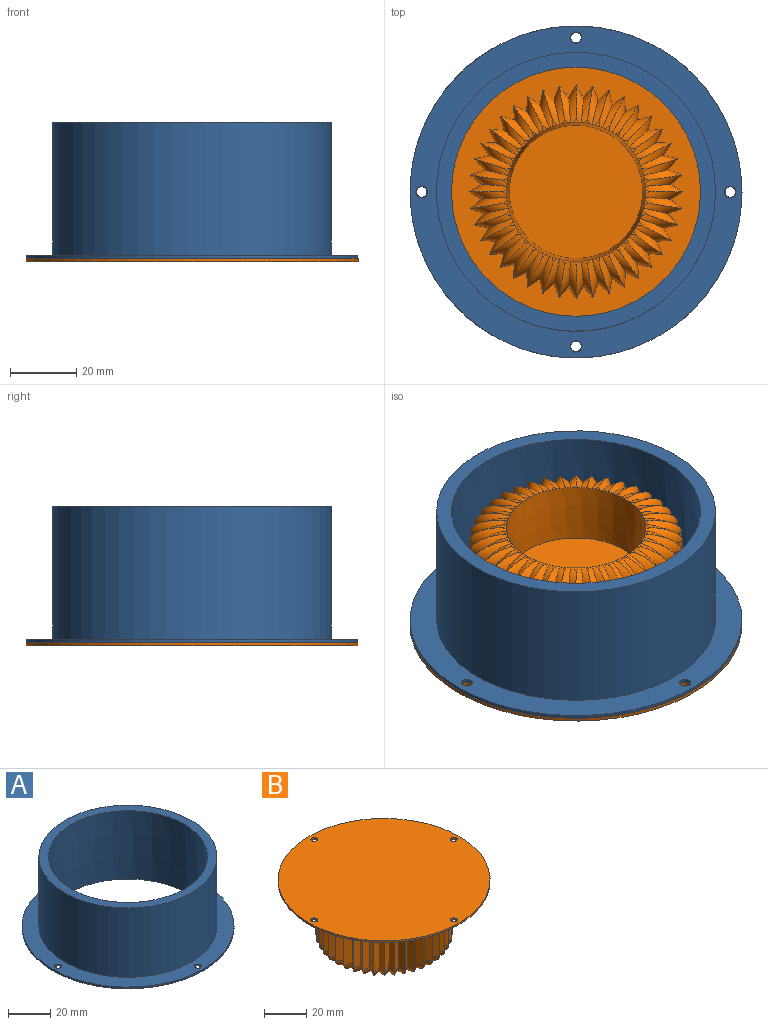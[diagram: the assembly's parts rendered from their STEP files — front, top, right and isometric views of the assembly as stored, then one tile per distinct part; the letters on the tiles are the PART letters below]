
ASSEMBLY  parts=2 mates=1
PART A: 10 faces, bbox 100x100x41 mm
  f0: cylinder r=42mm len=84mm, axis (0,0,-1), area 10555.8mm2, adj f1,f4
  f1: plane 84x84mm, normal (0,0,1), area 1123.9mm2, adj f0,f5
  f2: cylinder r=50mm len=100mm, axis (0,0,1), area 314.2mm2, adj f3,f4
  f3: plane 100x100mm, normal (0,0,-1), area 2879mm2, adj f2,f5,f6,f7,f8,f9
  f4: plane 100x100mm, normal (0,0,1), area 2275.9mm2, adj f0,f2,f6,f7,f8,f9
  f5: cone r=37.5mm half-angle=3deg, axis (0,0,-1), area 9950.8mm2, adj f1,f3
  f6: cylinder r=1.7mm len=3.4mm, axis (0,0,1), area 10.7mm2, adj f3,f4
  f7: cylinder r=1.7mm len=3.4mm, axis (0,0,1), area 10.7mm2, adj f3,f4
  f8: cylinder r=1.7mm len=3.4mm, axis (0,0,1), area 10.7mm2, adj f3,f4
  f9: cylinder r=1.7mm len=3.4mm, axis (0,0,1), area 10.7mm2, adj f3,f4
PART B: 289 faces, bbox 100x100x36 mm
  f0: cylinder r=1.6mm len=3.2mm, axis (0,0,1), area 10.1mm2, adj f285,f287
  f1: cylinder r=1.6mm len=3.2mm, axis (0,0,1), area 10.1mm2, adj f285,f287
  f2: cylinder r=1.6mm len=3.2mm, axis (0,0,1), area 10.1mm2, adj f285,f287
  f3: plane 1.37x1.29mm, normal (0,0,-1), area 0.8mm2, adj f199,f201,f283
  f4: plane 1.35x1.32mm, normal (0,0,-1), area 0.8mm2, adj f195,f197,f283
  f5: plane 1.38x1.23mm, normal (0,0,-1), area 0.8mm2, adj f191,f193,f283
  f6: plane 1.38x1.26mm, normal (0,0,-1), area 0.8mm2, adj f187,f189,f283
  f7: plane 1.34x1.34mm, normal (0,0,-1), area 0.8mm2, adj f183,f185,f283
  f8: plane 1.38x1.26mm, normal (0,0,-1), area 0.8mm2, adj f179,f181,f283
  f9: plane 1.38x1.23mm, normal (0,0,-1), area 0.8mm2, adj f175,f177,f283
  f10: plane 1.35x1.32mm, normal (0,0,-1), area 0.8mm2, adj f171,f173,f283
  f11: plane 1.37x1.29mm, normal (0,0,-1), area 0.8mm2, adj f167,f169,f283
  f12: plane 1.38x1.2mm, normal (0,0,-1), area 0.8mm2, adj f163,f165,f283
  f13: plane 1.37x1.29mm, normal (0,0,-1), area 0.8mm2, adj f159,f161,f283
  f14: plane 1.35x1.32mm, normal (0,0,-1), area 0.8mm2, adj f155,f157,f283
  f15: plane 1.38x1.23mm, normal (0,0,-1), area 0.8mm2, adj f151,f153,f283
  f16: plane 1.38x1.26mm, normal (0,0,-1), area 0.8mm2, adj f147,f149,f283
  f17: plane 1.34x1.34mm, normal (0,0,-1), area 0.8mm2, adj f143,f145,f283
  f18: plane 1.38x1.26mm, normal (0,0,-1), area 0.8mm2, adj f139,f141,f283
  f19: plane 1.38x1.23mm, normal (0,0,-1), area 0.8mm2, adj f135,f137,f283
  f20: plane 1.35x1.32mm, normal (0,0,-1), area 0.8mm2, adj f131,f133,f283
  f21: plane 1.37x1.29mm, normal (0,0,-1), area 0.8mm2, adj f127,f129,f283
  f22: plane 1.38x1.2mm, normal (0,0,-1), area 0.8mm2, adj f123,f125,f283
  f23: plane 1.37x1.29mm, normal (0,0,-1), area 0.8mm2, adj f124,f126,f283
  f24: plane 1.35x1.32mm, normal (0,0,-1), area 0.8mm2, adj f128,f130,f283
  f25: plane 1.38x1.23mm, normal (0,0,-1), area 0.8mm2, adj f132,f134,f283
  f26: plane 1.38x1.26mm, normal (0,0,-1), area 0.8mm2, adj f136,f138,f283
  f27: plane 1.34x1.34mm, normal (0,0,-1), area 0.8mm2, adj f140,f142,f283
  f28: plane 1.38x1.26mm, normal (0,0,-1), area 0.8mm2, adj f144,f146,f283
  f29: plane 1.38x1.23mm, normal (0,0,-1), area 0.8mm2, adj f148,f150,f283
  f30: plane 1.35x1.32mm, normal (0,0,-1), area 0.8mm2, adj f152,f154,f283
  f31: plane 1.37x1.29mm, normal (0,0,-1), area 0.8mm2, adj f156,f158,f283
  f32: plane 1.38x1.2mm, normal (0,0,-1), area 0.8mm2, adj f160,f162,f283
  f33: plane 1.37x1.29mm, normal (0,0,-1), area 0.8mm2, adj f164,f166,f283
  f34: plane 1.35x1.32mm, normal (0,0,-1), area 0.8mm2, adj f168,f170,f283
  f35: plane 1.38x1.23mm, normal (0,0,-1), area 0.8mm2, adj f172,f174,f283
  f36: plane 1.38x1.26mm, normal (0,0,-1), area 0.8mm2, adj f176,f178,f283
  f37: plane 1.34x1.34mm, normal (0,0,-1), area 0.8mm2, adj f180,f182,f283
  f38: plane 1.38x1.26mm, normal (0,0,-1), area 0.8mm2, adj f184,f186,f283
  f39: plane 1.38x1.23mm, normal (0,0,-1), area 0.8mm2, adj f188,f190,f283
  f40: plane 1.35x1.32mm, normal (0,0,-1), area 0.8mm2, adj f192,f194,f283
  f41: plane 1.37x1.29mm, normal (0,0,-1), area 0.8mm2, adj f196,f198,f283
  f42: plane 1.38x1.2mm, normal (0,0,-1), area 0.8mm2, adj f200,f202,f283
  f43: plane 25x3.86mm, normal (-0.5,-0.87,0), area 111.5mm2, adj f44,f122,f200,f280
  f44: plane 25x3.47mm, normal (-0.63,0.78,0), area 111.5mm2, adj f43,f45,f198,f278
  f45: plane 25x4.16mm, normal (-0.36,-0.93,0), area 111.5mm2, adj f44,f46,f196,f276
  f46: plane 25x3.31mm, normal (-0.74,0.67,0), area 111.5mm2, adj f45,f47,f194,f274
  f47: plane 25x4.36mm, normal (-0.21,-0.98,0), area 111.5mm2, adj f46,f48,f192,f272
  f48: plane 25x3.74mm, normal (-0.84,0.54,0), area 111.5mm2, adj f47,f49,f190,f270
  f49: plane 25x4.45mm, normal (-0.05,-1,0), area 111.5mm2, adj f48,f50,f188,f268
  f50: plane 25x4.07mm, normal (-0.91,0.41,0), area 111.5mm2, adj f49,f51,f186,f266
  f51: plane 25x4.43mm, normal (0.1,-0.99,0), area 111.5mm2, adj f50,f52,f184,f264
  f52: plane 25x4.31mm, normal (-0.97,0.26,0), area 111.5mm2, adj f51,f53,f182,f262
  f53: plane 25x4.31mm, normal (0.26,-0.97,0), area 111.5mm2, adj f52,f54,f180,f260
  f54: plane 25x4.43mm, normal (-0.99,0.1,0), area 111.5mm2, adj f53,f55,f178,f258
  f55: plane 25x4.07mm, normal (0.41,-0.91,0), area 111.5mm2, adj f54,f56,f176,f256
  f56: plane 25x4.45mm, normal (-1,-0.05,0), area 111.5mm2, adj f55,f57,f174,f254
  f57: plane 25x3.74mm, normal (0.54,-0.84,0), area 111.5mm2, adj f56,f58,f172,f252
  f58: plane 25x4.36mm, normal (-0.98,-0.21,0), area 111.5mm2, adj f57,f59,f170,f250
  f59: plane 25x3.31mm, normal (0.67,-0.74,0), area 111.5mm2, adj f58,f60,f168,f248
  f60: plane 25x4.16mm, normal (-0.93,-0.36,0), area 111.5mm2, adj f59,f61,f166,f246
  f61: plane 25x3.47mm, normal (0.78,-0.63,0), area 111.5mm2, adj f60,f62,f164,f244
  f62: plane 25x3.86mm, normal (-0.87,-0.5,0), area 111.5mm2, adj f61,f63,f162,f242
  f63: plane 25x3.86mm, normal (0.87,-0.5,0), area 111.5mm2, adj f62,f64,f160,f240
  f64: plane 25x3.47mm, normal (-0.78,-0.63,0), area 111.5mm2, adj f63,f65,f158,f238
  f65: plane 25x4.16mm, normal (0.93,-0.36,0), area 111.5mm2, adj f64,f66,f156,f236
  f66: plane 25x3.31mm, normal (-0.67,-0.74,0), area 111.5mm2, adj f65,f67,f154,f234
  f67: plane 25x4.36mm, normal (0.98,-0.21,0), area 111.5mm2, adj f66,f68,f152,f232
  f68: plane 25x3.74mm, normal (-0.54,-0.84,0), area 111.5mm2, adj f67,f69,f150,f230
  f69: plane 25x4.45mm, normal (1,-0.05,0), area 111.5mm2, adj f68,f70,f148,f228
  f70: plane 25x4.07mm, normal (-0.41,-0.91,0), area 111.5mm2, adj f69,f71,f146,f226
  f71: plane 25x4.43mm, normal (0.99,0.1,0), area 111.5mm2, adj f70,f72,f144,f224
  f72: plane 25x4.31mm, normal (-0.26,-0.97,0), area 111.5mm2, adj f71,f73,f142,f222
  f73: plane 25x4.31mm, normal (0.97,0.26,0), area 111.5mm2, adj f72,f74,f140,f220
  f74: plane 25x4.43mm, normal (-0.1,-0.99,0), area 111.5mm2, adj f73,f75,f138,f218
  f75: plane 25x4.07mm, normal (0.91,0.41,0), area 111.5mm2, adj f74,f76,f136,f216
  f76: plane 25x4.45mm, normal (0.05,-1,0), area 111.5mm2, adj f75,f77,f134,f214
  f77: plane 25x3.74mm, normal (0.84,0.54,0), area 111.5mm2, adj f76,f78,f132,f212
  f78: plane 25x4.36mm, normal (0.21,-0.98,0), area 111.5mm2, adj f77,f79,f130,f210
  f79: plane 25x3.31mm, normal (0.74,0.67,0), area 111.5mm2, adj f78,f80,f128,f208
  f80: plane 25x4.16mm, normal (0.36,-0.93,0), area 111.5mm2, adj f79,f81,f126,f206
  f81: plane 25x3.47mm, normal (0.63,0.78,0), area 111.5mm2, adj f80,f82,f124,f204
  f82: plane 25x3.86mm, normal (0.5,-0.87,0), area 111.5mm2, adj f81,f83,f123,f203
  f83: plane 25x3.86mm, normal (0.5,0.87,0), area 111.5mm2, adj f82,f84,f125,f205
  f84: plane 25x3.47mm, normal (0.63,-0.78,0), area 111.5mm2, adj f83,f85,f127,f207
  f85: plane 25x4.16mm, normal (0.36,0.93,0), area 111.5mm2, adj f84,f86,f129,f209
  f86: plane 25x3.31mm, normal (0.74,-0.67,0), area 111.5mm2, adj f85,f87,f131,f211
  f87: plane 25x4.36mm, normal (0.21,0.98,0), area 111.5mm2, adj f86,f88,f133,f213
  f88: plane 25x3.74mm, normal (0.84,-0.54,0), area 111.5mm2, adj f87,f89,f135,f215
  f89: plane 25x4.45mm, normal (0.05,1,0), area 111.5mm2, adj f88,f90,f137,f217
  f90: plane 25x4.07mm, normal (0.91,-0.41,0), area 111.5mm2, adj f89,f91,f139,f219
  f91: plane 25x4.43mm, normal (-0.1,0.99,0), area 111.5mm2, adj f90,f92,f141,f221
  f92: plane 25x4.31mm, normal (0.97,-0.26,0), area 111.5mm2, adj f91,f93,f143,f223
  f93: plane 25x4.31mm, normal (-0.26,0.97,0), area 111.5mm2, adj f92,f94,f145,f225
  f94: plane 25x4.43mm, normal (0.99,-0.1,0), area 111.5mm2, adj f93,f95,f147,f227
  f95: plane 25x4.07mm, normal (-0.41,0.91,0), area 111.5mm2, adj f94,f96,f149,f229
  f96: plane 25x4.45mm, normal (1,0.05,0), area 111.5mm2, adj f95,f97,f151,f231
  f97: plane 25x3.74mm, normal (-0.54,0.84,0), area 111.5mm2, adj f96,f98,f153,f233
  f98: plane 25x4.36mm, normal (0.98,0.21,0), area 111.5mm2, adj f97,f99,f155,f235
  f99: plane 25x3.31mm, normal (-0.67,0.74,0), area 111.5mm2, adj f98,f100,f157,f237
  f100: plane 25x4.16mm, normal (0.93,0.36,0), area 111.5mm2, adj f99,f101,f159,f239
  f101: plane 25x3.47mm, normal (-0.78,0.63,0), area 111.5mm2, adj f100,f102,f161,f241
  f102: plane 25x3.86mm, normal (0.87,0.5,0), area 111.5mm2, adj f101,f103,f163,f243
  f103: plane 25x3.86mm, normal (-0.87,0.5,0), area 111.5mm2, adj f102,f104,f165,f245
  f104: plane 25x3.47mm, normal (0.78,0.63,0), area 111.5mm2, adj f103,f105,f167,f247
  f105: plane 25x4.16mm, normal (-0.93,0.36,0), area 111.5mm2, adj f104,f106,f169,f249
  f106: plane 25x3.31mm, normal (0.67,0.74,0), area 111.5mm2, adj f105,f107,f171,f251
  f107: plane 25x4.36mm, normal (-0.98,0.21,0), area 111.5mm2, adj f106,f108,f173,f253
  f108: plane 25x3.74mm, normal (0.54,0.84,0), area 111.5mm2, adj f107,f109,f175,f255
  f109: plane 25x4.45mm, normal (-1,0.05,0), area 111.5mm2, adj f108,f110,f177,f257
  f110: plane 25x4.07mm, normal (0.41,0.91,0), area 111.5mm2, adj f109,f111,f179,f259
  f111: plane 25x4.43mm, normal (-0.99,-0.1,0), area 111.5mm2, adj f110,f112,f181,f261
  f112: plane 25x4.31mm, normal (0.26,0.97,0), area 111.5mm2, adj f111,f113,f183,f263
  f113: plane 25x4.31mm, normal (-0.97,-0.26,0), area 111.5mm2, adj f112,f114,f185,f265
  f114: plane 25x4.43mm, normal (0.1,0.99,0), area 111.5mm2, adj f113,f115,f187,f267
  f115: plane 25x4.07mm, normal (-0.91,-0.41,0), area 111.5mm2, adj f114,f116,f189,f269
  f116: plane 25x4.45mm, normal (-0.05,1,0), area 111.5mm2, adj f115,f117,f191,f271
  f117: plane 25x3.74mm, normal (-0.84,-0.54,0), area 111.5mm2, adj f116,f118,f193,f273
  f118: plane 25x4.36mm, normal (-0.21,0.98,0), area 111.5mm2, adj f117,f119,f195,f275
  f119: plane 25x3.31mm, normal (-0.74,-0.67,0), area 111.5mm2, adj f118,f120,f197,f277
  f120: plane 25x4.16mm, normal (-0.36,0.93,0), area 111.5mm2, adj f119,f121,f199,f279
  f121: plane 25x3.47mm, normal (-0.63,-0.78,0), area 111.5mm2, adj f120,f122,f201,f281
  f122: plane 25x3.86mm, normal (-0.5,0.87,0), area 111.5mm2, adj f43,f121,f202,f282
  f123: cylinder r=5mm len=11.65mm, axis (0.87,0.5,0), area 30.4mm2, adj f22,f82,f124,f125,f283
  f124: cylinder r=5mm len=11.36mm, axis (-0.78,0.63,0), area 30.4mm2, adj f23,f81,f123,f126,f283
  f125: cylinder r=5mm len=11.65mm, axis (-0.87,0.5,0), area 30.4mm2, adj f22,f83,f123,f127,f283
  f126: cylinder r=5mm len=11.66mm, axis (0.93,0.36,0), area 30.4mm2, adj f23,f80,f124,f128,f283
  f127: cylinder r=5mm len=11.36mm, axis (0.78,0.63,0), area 30.4mm2, adj f21,f84,f125,f129,f283
  f128: cylinder r=5mm len=11.2mm, axis (-0.67,0.74,0), area 30.4mm2, adj f24,f79,f126,f130,f283
  f129: cylinder r=5mm len=11.66mm, axis (-0.93,0.36,0), area 30.4mm2, adj f21,f85,f127,f131,f283
  f130: cylinder r=5mm len=11.38mm, axis (0.98,0.21,0), area 30.4mm2, adj f24,f78,f128,f132,f283
  f131: cylinder r=5mm len=11.2mm, axis (0.67,0.74,0), area 30.4mm2, adj f20,f86,f129,f133,f283
  f132: cylinder r=5mm len=11.59mm, axis (-0.54,0.84,0), area 30.4mm2, adj f25,f77,f130,f134,f283
  f133: cylinder r=5mm len=11.38mm, axis (-0.98,0.21,0), area 30.4mm2, adj f20,f87,f131,f135,f283
  f134: cylinder r=5mm len=10.82mm, axis (1,0.05,0), area 30.4mm2, adj f25,f76,f132,f136,f283
  f135: cylinder r=5mm len=11.59mm, axis (0.54,0.84,0), area 30.4mm2, adj f19,f88,f133,f137,f283
  f136: cylinder r=5mm len=11.69mm, axis (-0.41,0.91,0), area 30.4mm2, adj f26,f75,f134,f138,f283
  f137: cylinder r=5mm len=10.82mm, axis (-1,0.05,0), area 30.4mm2, adj f19,f89,f135,f139,f283
  f138: cylinder r=5mm len=11.04mm, axis (0.99,-0.1,0), area 30.4mm2, adj f26,f74,f136,f140,f283
  f139: cylinder r=5mm len=11.69mm, axis (0.41,0.91,0), area 30.4mm2, adj f18,f90,f137,f141,f283
  f140: cylinder r=5mm len=11.5mm, axis (-0.26,0.97,0), area 30.4mm2, adj f27,f73,f138,f142,f283
  f141: cylinder r=5mm len=11.04mm, axis (-0.99,-0.1,0), area 30.4mm2, adj f18,f91,f139,f143,f283
  f142: cylinder r=5mm len=11.5mm, axis (0.97,-0.26,0), area 30.4mm2, adj f27,f72,f140,f144,f283
  f143: cylinder r=5mm len=11.5mm, axis (0.26,0.97,0), area 30.4mm2, adj f17,f92,f141,f145,f283
  f144: cylinder r=5mm len=11.04mm, axis (-0.1,0.99,0), area 30.4mm2, adj f28,f71,f142,f146,f283
  f145: cylinder r=5mm len=11.5mm, axis (-0.97,-0.26,0), area 30.4mm2, adj f17,f93,f143,f147,f283
  f146: cylinder r=5mm len=11.69mm, axis (0.91,-0.41,0), area 30.4mm2, adj f28,f70,f144,f148,f283
  f147: cylinder r=5mm len=11.04mm, axis (0.1,0.99,0), area 30.4mm2, adj f16,f94,f145,f149,f283
  f148: cylinder r=5mm len=10.82mm, axis (0.05,1,0), area 30.4mm2, adj f29,f69,f146,f150,f283
  f149: cylinder r=5mm len=11.69mm, axis (-0.91,-0.41,0), area 30.4mm2, adj f16,f95,f147,f151,f283
  f150: cylinder r=5mm len=11.59mm, axis (0.84,-0.54,0), area 30.4mm2, adj f29,f68,f148,f152,f283
  f151: cylinder r=5mm len=10.82mm, axis (-0.05,1,0), area 30.4mm2, adj f15,f96,f149,f153,f283
  f152: cylinder r=5mm len=11.38mm, axis (0.21,0.98,0), area 30.4mm2, adj f30,f67,f150,f154,f283
  f153: cylinder r=5mm len=11.59mm, axis (-0.84,-0.54,0), area 30.4mm2, adj f15,f97,f151,f155,f283
  f154: cylinder r=5mm len=11.2mm, axis (0.74,-0.67,0), area 30.4mm2, adj f30,f66,f152,f156,f283
  f155: cylinder r=5mm len=11.38mm, axis (-0.21,0.98,0), area 30.4mm2, adj f14,f98,f153,f157,f283
  f156: cylinder r=5mm len=11.66mm, axis (0.36,0.93,0), area 30.4mm2, adj f31,f65,f154,f158,f283
  f157: cylinder r=5mm len=11.2mm, axis (-0.74,-0.67,0), area 30.4mm2, adj f14,f99,f155,f159,f283
  f158: cylinder r=5mm len=11.36mm, axis (0.63,-0.78,0), area 30.4mm2, adj f31,f64,f156,f160,f283
  f159: cylinder r=5mm len=11.66mm, axis (-0.36,0.93,0), area 30.4mm2, adj f13,f100,f157,f161,f283
  f160: cylinder r=5mm len=11.65mm, axis (0.5,0.87,0), area 30.4mm2, adj f32,f63,f158,f162,f283
  f161: cylinder r=5mm len=11.36mm, axis (-0.63,-0.78,0), area 30.4mm2, adj f13,f101,f159,f163,f283
  f162: cylinder r=5mm len=11.65mm, axis (0.5,-0.87,0), area 30.4mm2, adj f32,f62,f160,f164,f283
  f163: cylinder r=5mm len=11.65mm, axis (-0.5,0.87,0), area 30.4mm2, adj f12,f102,f161,f165,f283
  f164: cylinder r=5mm len=11.36mm, axis (0.63,0.78,0), area 30.4mm2, adj f33,f61,f162,f166,f283
  f165: cylinder r=5mm len=11.65mm, axis (-0.5,-0.87,0), area 30.4mm2, adj f12,f103,f163,f167,f283
  f166: cylinder r=5mm len=11.66mm, axis (0.36,-0.93,0), area 30.4mm2, adj f33,f60,f164,f168,f283
  f167: cylinder r=5mm len=11.36mm, axis (-0.63,0.78,0), area 30.4mm2, adj f11,f104,f165,f169,f283
  f168: cylinder r=5mm len=11.2mm, axis (0.74,0.67,0), area 30.4mm2, adj f34,f59,f166,f170,f283
  f169: cylinder r=5mm len=11.66mm, axis (-0.36,-0.93,0), area 30.4mm2, adj f11,f105,f167,f171,f283
  f170: cylinder r=5mm len=11.38mm, axis (0.21,-0.98,0), area 30.4mm2, adj f34,f58,f168,f172,f283
  f171: cylinder r=5mm len=11.2mm, axis (-0.74,0.67,0), area 30.4mm2, adj f10,f106,f169,f173,f283
  f172: cylinder r=5mm len=11.59mm, axis (0.84,0.54,0), area 30.4mm2, adj f35,f57,f170,f174,f283
  f173: cylinder r=5mm len=11.38mm, axis (-0.21,-0.98,0), area 30.4mm2, adj f10,f107,f171,f175,f283
  f174: cylinder r=5mm len=10.82mm, axis (0.05,-1,0), area 30.4mm2, adj f35,f56,f172,f176,f283
  f175: cylinder r=5mm len=11.59mm, axis (-0.84,0.54,0), area 30.4mm2, adj f9,f108,f173,f177,f283
  f176: cylinder r=5mm len=11.69mm, axis (0.91,0.41,0), area 30.4mm2, adj f36,f55,f174,f178,f283
  f177: cylinder r=5mm len=10.82mm, axis (-0.05,-1,0), area 30.4mm2, adj f9,f109,f175,f179,f283
  f178: cylinder r=5mm len=11.04mm, axis (-0.1,-0.99,0), area 30.4mm2, adj f36,f54,f176,f180,f283
  f179: cylinder r=5mm len=11.69mm, axis (-0.91,0.41,0), area 30.4mm2, adj f8,f110,f177,f181,f283
  f180: cylinder r=5mm len=11.5mm, axis (0.97,0.26,0), area 30.4mm2, adj f37,f53,f178,f182,f283
  f181: cylinder r=5mm len=11.04mm, axis (0.1,-0.99,0), area 30.4mm2, adj f8,f111,f179,f183,f283
  f182: cylinder r=5mm len=11.5mm, axis (-0.26,-0.97,0), area 30.4mm2, adj f37,f52,f180,f184,f283
  f183: cylinder r=5mm len=11.5mm, axis (-0.97,0.26,0), area 30.4mm2, adj f7,f112,f181,f185,f283
  f184: cylinder r=5mm len=11.04mm, axis (0.99,0.1,0), area 30.4mm2, adj f38,f51,f182,f186,f283
  f185: cylinder r=5mm len=11.5mm, axis (0.26,-0.97,0), area 30.4mm2, adj f7,f113,f183,f187,f283
  f186: cylinder r=5mm len=11.69mm, axis (-0.41,-0.91,0), area 30.4mm2, adj f38,f50,f184,f188,f283
  f187: cylinder r=5mm len=11.04mm, axis (-0.99,0.1,0), area 30.4mm2, adj f6,f114,f185,f189,f283
  f188: cylinder r=5mm len=10.82mm, axis (1,-0.05,0), area 30.4mm2, adj f39,f49,f186,f190,f283
  f189: cylinder r=5mm len=11.69mm, axis (0.41,-0.91,0), area 30.4mm2, adj f6,f115,f187,f191,f283
  f190: cylinder r=5mm len=11.59mm, axis (-0.54,-0.84,0), area 30.4mm2, adj f39,f48,f188,f192,f283
  f191: cylinder r=5mm len=10.82mm, axis (-1,-0.05,0), area 30.4mm2, adj f5,f116,f189,f193,f283
  f192: cylinder r=5mm len=11.38mm, axis (0.98,-0.21,0), area 30.4mm2, adj f40,f47,f190,f194,f283
  f193: cylinder r=5mm len=11.59mm, axis (0.54,-0.84,0), area 30.4mm2, adj f5,f117,f191,f195,f283
  f194: cylinder r=5mm len=11.2mm, axis (-0.67,-0.74,0), area 30.4mm2, adj f40,f46,f192,f196,f283
  f195: cylinder r=5mm len=11.38mm, axis (-0.98,-0.21,0), area 30.4mm2, adj f4,f118,f193,f197,f283
  f196: cylinder r=5mm len=11.66mm, axis (0.93,-0.36,0), area 30.4mm2, adj f41,f45,f194,f198,f283
  f197: cylinder r=5mm len=11.2mm, axis (0.67,-0.74,0), area 30.4mm2, adj f4,f119,f195,f199,f283
  f198: cylinder r=5mm len=11.36mm, axis (-0.78,-0.63,0), area 30.4mm2, adj f41,f44,f196,f200,f283
  f199: cylinder r=5mm len=11.66mm, axis (-0.93,-0.36,0), area 30.4mm2, adj f3,f120,f197,f201,f283
  f200: cylinder r=5mm len=11.65mm, axis (0.87,-0.5,0), area 30.4mm2, adj f42,f43,f198,f202,f283
  f201: cylinder r=5mm len=11.36mm, axis (0.78,-0.63,0), area 30.4mm2, adj f3,f121,f199,f202,f283
  f202: cylinder r=5mm len=11.65mm, axis (-0.87,-0.5,0), area 30.4mm2, adj f42,f122,f200,f201,f283
  f203: cylinder r=5mm len=12.66mm, axis (-0.87,-0.5,0), area 31.1mm2, adj f82,f204,f205,f285
  f204: cylinder r=5mm len=12.27mm, axis (0.78,-0.63,0), area 31.1mm2, adj f81,f203,f206,f285
  f205: cylinder r=5mm len=12.66mm, axis (0.87,-0.5,0), area 31.1mm2, adj f83,f203,f207,f285
  f206: cylinder r=5mm len=12.75mm, axis (-0.93,-0.36,0), area 31.1mm2, adj f80,f204,f208,f285
  f207: cylinder r=5mm len=12.27mm, axis (-0.78,-0.63,0), area 31.1mm2, adj f84,f205,f209,f285
  f208: cylinder r=5mm len=12.07mm, axis (0.67,-0.74,0), area 31.1mm2, adj f79,f206,f210,f285
  f209: cylinder r=5mm len=12.75mm, axis (0.93,-0.36,0), area 31.1mm2, adj f85,f207,f211,f285
  f210: cylinder r=5mm len=12.52mm, axis (-0.98,-0.21,0), area 31.1mm2, adj f78,f208,f212,f285
  f211: cylinder r=5mm len=12.07mm, axis (-0.67,-0.74,0), area 31.1mm2, adj f86,f209,f213,f285
  f212: cylinder r=5mm len=12.56mm, axis (0.54,-0.84,0), area 31.1mm2, adj f77,f210,f214,f285
  f213: cylinder r=5mm len=12.52mm, axis (0.98,-0.21,0), area 31.1mm2, adj f87,f211,f215,f285
  f214: cylinder r=5mm len=11.98mm, axis (-1,-0.05,0), area 31.1mm2, adj f76,f212,f216,f285
  f215: cylinder r=5mm len=12.56mm, axis (-0.54,-0.84,0), area 31.1mm2, adj f88,f213,f217,f285
  f216: cylinder r=5mm len=12.75mm, axis (0.41,-0.91,0), area 31.1mm2, adj f75,f214,f218,f285
  f217: cylinder r=5mm len=11.98mm, axis (1,-0.05,0), area 31.1mm2, adj f89,f215,f219,f285
  f218: cylinder r=5mm len=12.19mm, axis (-0.99,0.1,0), area 31.1mm2, adj f74,f216,f220,f285
  f219: cylinder r=5mm len=12.75mm, axis (-0.41,-0.91,0), area 31.1mm2, adj f90,f217,f221,f285
  f220: cylinder r=5mm len=12.63mm, axis (0.26,-0.97,0), area 31.1mm2, adj f73,f218,f222,f285
  f221: cylinder r=5mm len=12.19mm, axis (0.99,0.1,0), area 31.1mm2, adj f91,f219,f223,f285
  f222: cylinder r=5mm len=12.63mm, axis (-0.97,0.26,0), area 31.1mm2, adj f72,f220,f224,f285
  f223: cylinder r=5mm len=12.63mm, axis (-0.26,-0.97,0), area 31.1mm2, adj f92,f221,f225,f285
  f224: cylinder r=5mm len=12.19mm, axis (0.1,-0.99,0), area 31.1mm2, adj f71,f222,f226,f285
  f225: cylinder r=5mm len=12.63mm, axis (0.97,0.26,0), area 31.1mm2, adj f93,f223,f227,f285
  f226: cylinder r=5mm len=12.75mm, axis (-0.91,0.41,0), area 31.1mm2, adj f70,f224,f228,f285
  f227: cylinder r=5mm len=12.19mm, axis (-0.1,-0.99,0), area 31.1mm2, adj f94,f225,f229,f285
  f228: cylinder r=5mm len=11.98mm, axis (-0.05,-1,0), area 31.1mm2, adj f69,f226,f230,f285
  f229: cylinder r=5mm len=12.75mm, axis (0.91,0.41,0), area 31.1mm2, adj f95,f227,f231,f285
  f230: cylinder r=5mm len=12.56mm, axis (-0.84,0.54,0), area 31.1mm2, adj f68,f228,f232,f285
  f231: cylinder r=5mm len=11.98mm, axis (0.05,-1,0), area 31.1mm2, adj f96,f229,f233,f285
  f232: cylinder r=5mm len=12.52mm, axis (-0.21,-0.98,0), area 31.1mm2, adj f67,f230,f234,f285
  f233: cylinder r=5mm len=12.56mm, axis (0.84,0.54,0), area 31.1mm2, adj f97,f231,f235,f285
  f234: cylinder r=5mm len=12.07mm, axis (-0.74,0.67,0), area 31.1mm2, adj f66,f232,f236,f285
  f235: cylinder r=5mm len=12.52mm, axis (0.21,-0.98,0), area 31.1mm2, adj f98,f233,f237,f285
  f236: cylinder r=5mm len=12.75mm, axis (-0.36,-0.93,0), area 31.1mm2, adj f65,f234,f238,f285
  f237: cylinder r=5mm len=12.07mm, axis (0.74,0.67,0), area 31.1mm2, adj f99,f235,f239,f285
  f238: cylinder r=5mm len=12.27mm, axis (-0.63,0.78,0), area 31.1mm2, adj f64,f236,f240,f285
  f239: cylinder r=5mm len=12.75mm, axis (0.36,-0.93,0), area 31.1mm2, adj f100,f237,f241,f285
  f240: cylinder r=5mm len=12.66mm, axis (-0.5,-0.87,0), area 31.1mm2, adj f63,f238,f242,f285
  f241: cylinder r=5mm len=12.27mm, axis (0.63,0.78,0), area 31.1mm2, adj f101,f239,f243,f285
  f242: cylinder r=5mm len=12.66mm, axis (-0.5,0.87,0), area 31.1mm2, adj f62,f240,f244,f285
  f243: cylinder r=5mm len=12.66mm, axis (0.5,-0.87,0), area 31.1mm2, adj f102,f241,f245,f285
  f244: cylinder r=5mm len=12.27mm, axis (-0.63,-0.78,0), area 31.1mm2, adj f61,f242,f246,f285
  f245: cylinder r=5mm len=12.66mm, axis (0.5,0.87,0), area 31.1mm2, adj f103,f243,f247,f285
  f246: cylinder r=5mm len=12.75mm, axis (-0.36,0.93,0), area 31.1mm2, adj f60,f244,f248,f285
  f247: cylinder r=5mm len=12.27mm, axis (0.63,-0.78,0), area 31.1mm2, adj f104,f245,f249,f285
  f248: cylinder r=5mm len=12.07mm, axis (-0.74,-0.67,0), area 31.1mm2, adj f59,f246,f250,f285
  f249: cylinder r=5mm len=12.75mm, axis (0.36,0.93,0), area 31.1mm2, adj f105,f247,f251,f285
  f250: cylinder r=5mm len=12.52mm, axis (-0.21,0.98,0), area 31.1mm2, adj f58,f248,f252,f285
  f251: cylinder r=5mm len=12.07mm, axis (0.74,-0.67,0), area 31.1mm2, adj f106,f249,f253,f285
  f252: cylinder r=5mm len=12.56mm, axis (-0.84,-0.54,0), area 31.1mm2, adj f57,f250,f254,f285
  f253: cylinder r=5mm len=12.52mm, axis (0.21,0.98,0), area 31.1mm2, adj f107,f251,f255,f285
  f254: cylinder r=5mm len=11.98mm, axis (-0.05,1,0), area 31.1mm2, adj f56,f252,f256,f285
  f255: cylinder r=5mm len=12.56mm, axis (0.84,-0.54,0), area 31.1mm2, adj f108,f253,f257,f285
  f256: cylinder r=5mm len=12.75mm, axis (-0.91,-0.41,0), area 31.1mm2, adj f55,f254,f258,f285
  f257: cylinder r=5mm len=11.98mm, axis (0.05,1,0), area 31.1mm2, adj f109,f255,f259,f285
  f258: cylinder r=5mm len=12.19mm, axis (0.1,0.99,0), area 31.1mm2, adj f54,f256,f260,f285
  f259: cylinder r=5mm len=12.75mm, axis (0.91,-0.41,0), area 31.1mm2, adj f110,f257,f261,f285
  f260: cylinder r=5mm len=12.63mm, axis (-0.97,-0.26,0), area 31.1mm2, adj f53,f258,f262,f285
  f261: cylinder r=5mm len=12.19mm, axis (-0.1,0.99,0), area 31.1mm2, adj f111,f259,f263,f285
  f262: cylinder r=5mm len=12.63mm, axis (0.26,0.97,0), area 31.1mm2, adj f52,f260,f264,f285
  f263: cylinder r=5mm len=12.63mm, axis (0.97,-0.26,0), area 31.1mm2, adj f112,f261,f265,f285
  f264: cylinder r=5mm len=12.19mm, axis (-0.99,-0.1,0), area 31.1mm2, adj f51,f262,f266,f285
  f265: cylinder r=5mm len=12.63mm, axis (-0.26,0.97,0), area 31.1mm2, adj f113,f263,f267,f285
  f266: cylinder r=5mm len=12.75mm, axis (0.41,0.91,0), area 31.1mm2, adj f50,f264,f268,f285
  f267: cylinder r=5mm len=12.19mm, axis (0.99,-0.1,0), area 31.1mm2, adj f114,f265,f269,f285
  f268: cylinder r=5mm len=11.98mm, axis (-1,0.05,0), area 31.1mm2, adj f49,f266,f270,f285
  f269: cylinder r=5mm len=12.75mm, axis (-0.41,0.91,0), area 31.1mm2, adj f115,f267,f271,f285
  f270: cylinder r=5mm len=12.56mm, axis (0.54,0.84,0), area 31.1mm2, adj f48,f268,f272,f285
  f271: cylinder r=5mm len=11.98mm, axis (1,0.05,0), area 31.1mm2, adj f116,f269,f273,f285
  f272: cylinder r=5mm len=12.52mm, axis (-0.98,0.21,0), area 31.1mm2, adj f47,f270,f274,f285
  f273: cylinder r=5mm len=12.56mm, axis (-0.54,0.84,0), area 31.1mm2, adj f117,f271,f275,f285
  f274: cylinder r=5mm len=12.07mm, axis (0.67,0.74,0), area 31.1mm2, adj f46,f272,f276,f285
  f275: cylinder r=5mm len=12.52mm, axis (0.98,0.21,0), area 31.1mm2, adj f118,f273,f277,f285
  f276: cylinder r=5mm len=12.75mm, axis (-0.93,0.36,0), area 31.1mm2, adj f45,f274,f278,f285
  f277: cylinder r=5mm len=12.07mm, axis (-0.67,0.74,0), area 31.1mm2, adj f119,f275,f279,f285
  f278: cylinder r=5mm len=12.27mm, axis (0.78,0.63,0), area 31.1mm2, adj f44,f276,f280,f285
  f279: cylinder r=5mm len=12.75mm, axis (0.93,0.36,0), area 31.1mm2, adj f120,f277,f281,f285
  f280: cylinder r=5mm len=12.66mm, axis (-0.87,0.5,0), area 31.1mm2, adj f43,f278,f282,f285
  f281: cylinder r=5mm len=12.27mm, axis (-0.78,0.63,0), area 31.1mm2, adj f121,f279,f282,f285
  f282: cylinder r=5mm len=12.66mm, axis (0.87,0.5,0), area 31.1mm2, adj f122,f280,f281,f285
  f283: cone r=21mm half-angle=3deg, axis (0,0,-1), area 2322.4mm2, adj f3,f4,f5,f6,f7,f8,f9,f10
  f284: plane 40.11x40.11mm, normal (0,0,-1), area 1263.8mm2, adj f283
  f285: plane 100x100mm, normal (0,0,-1), area 6458.1mm2, adj f0,f1,f2,f203,f204,f205,f206,f207
  f286: cylinder r=50mm len=100mm, axis (0,0,-1), area 314.2mm2, adj f285,f287
  f287: plane 100x100mm, normal (0,0,1), area 7821.8mm2, adj f0,f1,f2,f286,f288
  f288: cylinder r=1.6mm len=3.2mm, axis (0,0,1), area 10.1mm2, adj f285,f287
PLACE A t=(-154.85,-70.74,6.74)mm
PLACE B rot(axis=(1,0,0),180deg) t=(-154.85,-70.74,40.74)mm
MATE parallel A.f8 <-> B.f2  axis (0,0,-1) through (-108.35,-70.74,5.74)mm
